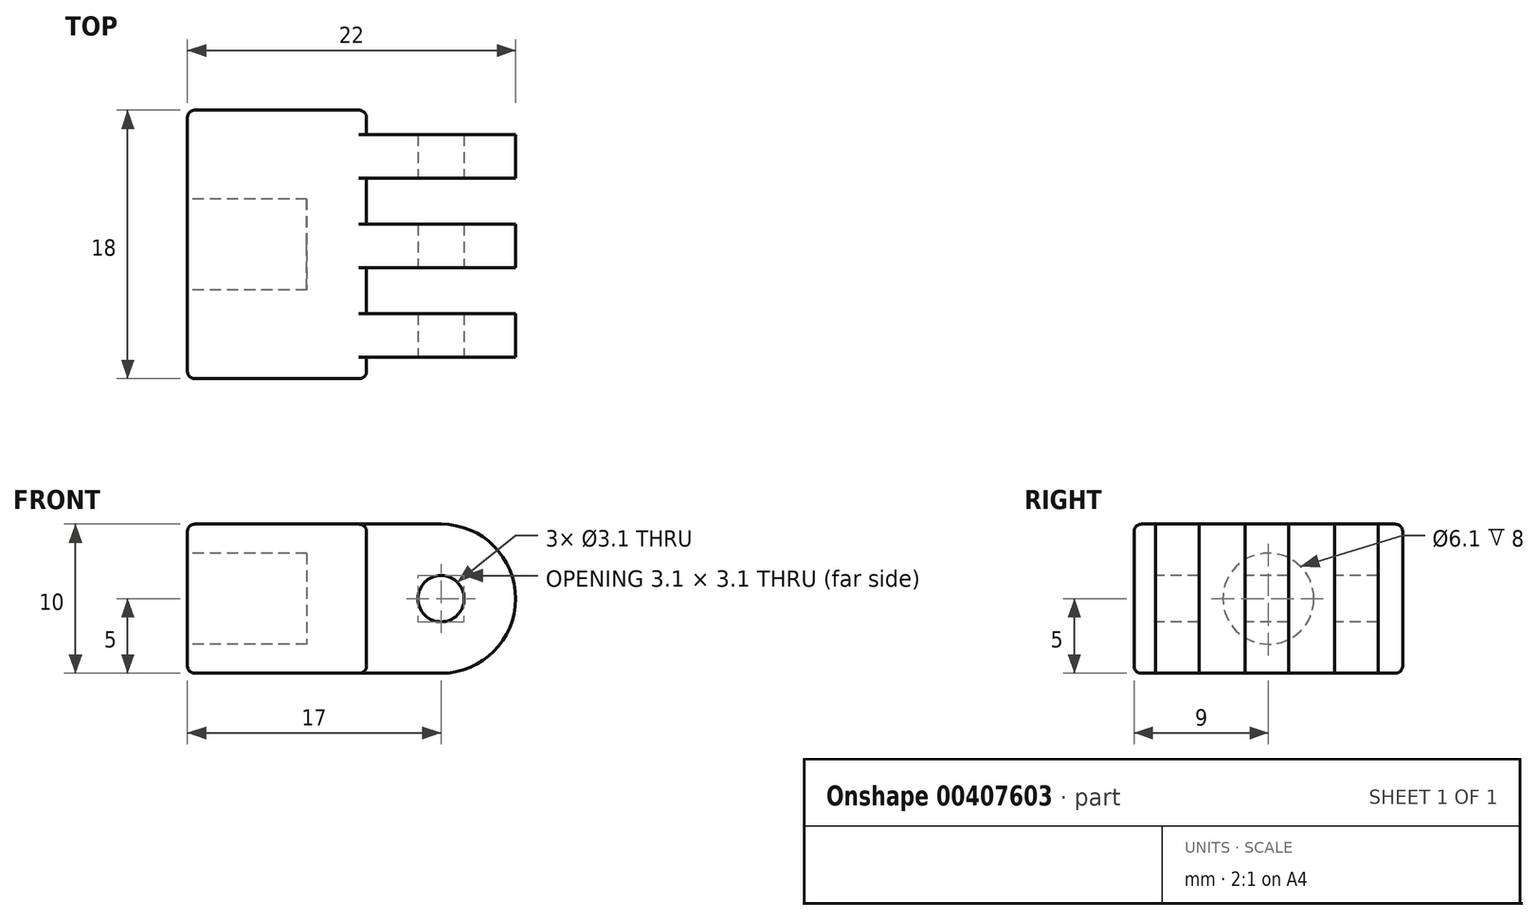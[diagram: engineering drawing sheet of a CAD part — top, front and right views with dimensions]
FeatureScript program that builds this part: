
annotation { "Feature Type Name" : "Feature", "Feature Type Description" : "" }
export const myFeature = defineFeature(function(context is Context, id is Id, definition is map)
    precondition{}
    {
        {
            var Q0;
            Q0=qCreatedBy(makeId("Top.planeOp"),FACE);
            var sketch = newSketch(context, id + "F0", { "sketchPlane" : qUnion([Q0])});
            skLineSegment(sketch, "E0.bottom", {"start": v(-6, 9) * mm, "end": v(6, 9) * mm});
            skLineSegment(sketch, "E0.top", {"start": v(-6, -9) * mm, "end": v(6, -9) * mm});
            skLineSegment(sketch, "E0.left", {"start": v(-6, 9) * mm, "end": v(-6, -9) * mm});
            skLineSegment(sketch, "E0.right", {"start": v(6, 9) * mm, "end": v(6, -9) * mm});
            skPoint(sketch, "E0.middle", {"position": v(0, 0) * mm});
            skLineSegment(sketch, "E1", {"start": v(0, 0) * mm, "end": v(19.14, 0) * mm, "construction": true});
            skLineSegment(sketch, "E2", {"start": v(6, 1.35) * mm, "end": v(16, 1.35) * mm});
            skLineSegment(sketch, "E3", {"start": v(16, 1.35) * mm, "end": v(16, -1.55) * mm});
            skLineSegment(sketch, "E4", {"start": v(16, -1.55) * mm, "end": v(6, -1.55) * mm});
            skLineSegment(sketch, "E5", {"start": v(6, 4.45) * mm, "end": v(16, 4.45) * mm});
            skLineSegment(sketch, "E6", {"start": v(16, 4.45) * mm, "end": v(16, 7.35) * mm});
            skLineSegment(sketch, "E7", {"start": v(16, 7.35) * mm, "end": v(6, 7.35) * mm});
            skLineSegment(sketch, "E8", {"start": v(6, -4.65) * mm, "end": v(16, -4.65) * mm});
            skLineSegment(sketch, "E9", {"start": v(16, -4.65) * mm, "end": v(16, -7.55) * mm});
            skLineSegment(sketch, "E10", {"start": v(16, -7.55) * mm, "end": v(6, -7.55) * mm});
            skSolve(sketch);
        }
        {
            var Q0;
            {var subQ1=sQuery(id+"F0.wireOp",EDGE,"E0.bottom");Q0=makeQuery(id+"F0.imprint","IMPRINT",FACE,{"disambiguationData":[TD([[makeQuery(id+"F0.imprint","IMPRINT",EDGE,{"derivedFrom":subQ1}),-1.0]])]});}
            var Q1;
            {var subQ0=sQuery(id+"F0.wireOp",EDGE,"E5");Q1=makeQuery(id+"F0.imprint","IMPRINT",FACE,{"disambiguationData":[TD([[makeQuery(id+"F0.imprint","IMPRINT",EDGE,{"derivedFrom":subQ0}),1.0]])]});}
            var Q2;
            {var subQ0=sQuery(id+"F0.wireOp",EDGE,"E2");Q2=makeQuery(id+"F0.imprint","IMPRINT",FACE,{"disambiguationData":[TD([[makeQuery(id+"F0.imprint","IMPRINT",EDGE,{"derivedFrom":subQ0}),-1.0]])]});}
            var Q3;
            {var subQ0=sQuery(id+"F0.wireOp",EDGE,"E8");Q3=makeQuery(id+"F0.imprint","IMPRINT",FACE,{"disambiguationData":[TD([[makeQuery(id+"F0.imprint","IMPRINT",EDGE,{"derivedFrom":subQ0}),-1.0]])]});}
            extrude(context, id + "F1", {"entities" : qUnion([Q0, Q1, Q2, Q3]), "depth" : 10 * mm});
        }
        {
            var Q0;
            Q0=makeQuery(id+"F1.opExtrude","SWEPT_FACE",FACE,{"disambiguationData":[OSD([sQuery(id+"F0.wireOp",EDGE,"E0.left")])]});
            var sketch = newSketch(context, id + "F2", { "sketchPlane" : qUnion([Q0])});
            skLineSegment(sketch, "E11", {"start": v(0, 0) * mm, "end": v(0, 10) * mm, "construction": true});
            skLineSegment(sketch, "E12", {"start": v(9, 5) * mm, "end": v(-9, 5) * mm, "construction": true});
            skCircle(sketch, "E13", {"center": v(0, 5) * mm, "radius": 3.05 * mm});
            skSolve(sketch);
        }
        {
            var Q0;
            Q0=makeQuery(id+"F2.imprint","IMPRINT",FACE,{"disambiguationData":[TD([[makeQuery(id+"F2.imprint","IMPRINT",EDGE,{"derivedFrom":sQuery(id+"F2.wireOp",EDGE,"E13")}),1.0]])]});
            extrude(context, id + "F3", {"entities" : qUnion([Q0]), "operationType" : NewBodyOperationType.REMOVE, "oppositeDirection" : true, "depth" : 8 * mm});
        }
        {
            var Q0;
            Q0=makeQuery(id+"F1.opExtrude","SWEPT_FACE",FACE,{"disambiguationData":[OSD([sQuery(id+"F0.wireOp",EDGE,"E10")])]});
            var sketch = newSketch(context, id + "F4", { "sketchPlane" : qUnion([Q0])});
            skLineSegment(sketch, "E14", {"start": v(11, 0) * mm, "end": v(11, 10) * mm, "construction": true});
            skLineSegment(sketch, "E15", {"start": v(16, 5) * mm, "end": v(6, 5) * mm, "construction": true});
            skCircle(sketch, "E16", {"center": v(11, 5) * mm, "radius": 1.55 * mm});
            skSolve(sketch);
        }
        {
            var Q0;
            Q0=makeQuery(id+"F4.imprint","IMPRINT",FACE,{"disambiguationData":[TD([[makeQuery(id+"F4.imprint","IMPRINT",EDGE,{"derivedFrom":sQuery(id+"F4.wireOp",EDGE,"E16")}),1.0]])]});
            extrude(context, id + "F5", {"entities" : qUnion([Q0]), "operationType" : NewBodyOperationType.REMOVE, "oppositeDirection" : true, "depth" : 25 * mm});
        }
        {
            var Q0;
            Q0=makeQuery(id+"F1.opExtrude","CAP_EDGE",EDGE,{"disambiguationData":[OSD([sQuery(id+"F0.wireOp",EDGE,"E0.left")])],"isStart":false});
            var Q1;
            Q1=makeQuery(id+"F1.opExtrude","CAP_EDGE",EDGE,{"disambiguationData":[OSD([sQuery(id+"F0.wireOp",EDGE,"E0.top")])],"isStart":false});
            var Q2;
            Q2=makeQuery(id+"F1.opExtrude","CAP_EDGE",EDGE,{"disambiguationData":[OSD([sQuery(id+"F0.wireOp",EDGE,"E0.bottom")])],"isStart":false});
            var Q3;
            Q3=makeQuery(id+"F1.opExtrude","SWEPT_EDGE",EDGE,{"disambiguationData":[OSD([sQuery(id+"F0.wireOp",EDGE,"E0.top"),sQuery(id+"F0.wireOp",EDGE,"E0.left")])]});
            var Q4;
            Q4=makeQuery(id+"F1.opExtrude","CAP_EDGE",EDGE,{"disambiguationData":[OSD([sQuery(id+"F0.wireOp",EDGE,"E0.left")])],"isStart":true});
            var Q5;
            Q5=makeQuery(id+"F1.opExtrude","SWEPT_EDGE",EDGE,{"disambiguationData":[OSD([sQuery(id+"F0.wireOp",EDGE,"E0.bottom"),sQuery(id+"F0.wireOp",EDGE,"E0.left")])]});
            var Q6;
            Q6=makeQuery(id+"F1.opExtrude","CAP_EDGE",EDGE,{"disambiguationData":[OSD([sQuery(id+"F0.wireOp",EDGE,"E0.bottom")])],"isStart":true});
            var Q7;
            Q7=makeQuery(id+"F1.opExtrude","CAP_EDGE",EDGE,{"disambiguationData":[OSD([sQuery(id+"F0.wireOp",EDGE,"E0.top")])],"isStart":true});
            var Q8;
            Q8=makeQuery(id+"F1.opExtrude","SWEPT_EDGE",EDGE,{"disambiguationData":[OSD([sQuery(id+"F0.wireOp",EDGE,"E0.top"),sQuery(id+"F0.wireOp",EDGE,"E0.right")])]});
            var Q9;
            {var subQ0=sQuery(id+"F0.wireOp",EDGE,"E0.right");Q9=makeQuery(id+"F1.opExtrude","CAP_EDGE",EDGE,{"disambiguationData":[OSD([subQ0]),TDD([makeQuery(id+"F0.imprint","IMPRINT",EDGE,{"disambiguationData":[TD([[makeQuery(id+"F0.imprint","INTERSECT",VERTEX,{"derivedFrom":[sQuery(id+"F0.wireOp",EDGE,"E0.top"),subQ0]}),1.0]])],"derivedFrom":subQ0})])],"isStart":true});}
            var Q10;
            {var subQ0=sQuery(id+"F0.wireOp",EDGE,"E0.right");Q10=makeQuery(id+"F1.opExtrude","CAP_EDGE",EDGE,{"disambiguationData":[OSD([subQ0]),TDD([makeQuery(id+"F0.imprint","IMPRINT",EDGE,{"disambiguationData":[TD([[makeQuery(id+"F0.imprint","INTERSECT",VERTEX,{"derivedFrom":[subQ0,sQuery(id+"F0.wireOp",EDGE,"E4")]}),-1.0]])],"derivedFrom":subQ0})])],"isStart":true});}
            var Q11;
            {var subQ0=sQuery(id+"F0.wireOp",EDGE,"E0.right");Q11=makeQuery(id+"F1.opExtrude","CAP_EDGE",EDGE,{"disambiguationData":[OSD([subQ0]),TDD([makeQuery(id+"F0.imprint","IMPRINT",EDGE,{"disambiguationData":[TD([[makeQuery(id+"F0.imprint","INTERSECT",VERTEX,{"derivedFrom":[subQ0,sQuery(id+"F0.wireOp",EDGE,"E2")]}),1.0]])],"derivedFrom":subQ0})])],"isStart":true});}
            var Q12;
            {var subQ0=sQuery(id+"F0.wireOp",EDGE,"E0.right");Q12=makeQuery(id+"F1.opExtrude","CAP_EDGE",EDGE,{"disambiguationData":[OSD([subQ0]),TDD([makeQuery(id+"F0.imprint","IMPRINT",EDGE,{"disambiguationData":[TD([[makeQuery(id+"F0.imprint","INTERSECT",VERTEX,{"derivedFrom":[sQuery(id+"F0.wireOp",EDGE,"E0.bottom"),subQ0]}),-1.0]])],"derivedFrom":subQ0})])],"isStart":true});}
            var Q13;
            Q13=makeQuery(id+"F1.opExtrude","SWEPT_EDGE",EDGE,{"disambiguationData":[OSD([sQuery(id+"F0.wireOp",EDGE,"E0.bottom"),sQuery(id+"F0.wireOp",EDGE,"E0.right")])]});
            var Q14;
            {var subQ0=sQuery(id+"F0.wireOp",EDGE,"E0.right");Q14=makeQuery(id+"F1.opExtrude","CAP_EDGE",EDGE,{"disambiguationData":[OSD([subQ0]),TDD([makeQuery(id+"F0.imprint","IMPRINT",EDGE,{"disambiguationData":[TD([[makeQuery(id+"F0.imprint","INTERSECT",VERTEX,{"derivedFrom":[sQuery(id+"F0.wireOp",EDGE,"E0.bottom"),subQ0]}),-1.0]])],"derivedFrom":subQ0})])],"isStart":false});}
            var Q15;
            {var subQ0=sQuery(id+"F0.wireOp",EDGE,"E0.right");Q15=makeQuery(id+"F1.opExtrude","CAP_EDGE",EDGE,{"disambiguationData":[OSD([subQ0]),TDD([makeQuery(id+"F0.imprint","IMPRINT",EDGE,{"disambiguationData":[TD([[makeQuery(id+"F0.imprint","INTERSECT",VERTEX,{"derivedFrom":[subQ0,sQuery(id+"F0.wireOp",EDGE,"E2")]}),1.0]])],"derivedFrom":subQ0})])],"isStart":false});}
            var Q16;
            {var subQ0=sQuery(id+"F0.wireOp",EDGE,"E0.right");Q16=makeQuery(id+"F1.opExtrude","CAP_EDGE",EDGE,{"disambiguationData":[OSD([subQ0]),TDD([makeQuery(id+"F0.imprint","IMPRINT",EDGE,{"disambiguationData":[TD([[makeQuery(id+"F0.imprint","INTERSECT",VERTEX,{"derivedFrom":[subQ0,sQuery(id+"F0.wireOp",EDGE,"E4")]}),-1.0]])],"derivedFrom":subQ0})])],"isStart":false});}
            var Q17;
            {var subQ0=sQuery(id+"F0.wireOp",EDGE,"E0.right");Q17=makeQuery(id+"F1.opExtrude","CAP_EDGE",EDGE,{"disambiguationData":[OSD([subQ0]),TDD([makeQuery(id+"F0.imprint","IMPRINT",EDGE,{"disambiguationData":[TD([[makeQuery(id+"F0.imprint","INTERSECT",VERTEX,{"derivedFrom":[sQuery(id+"F0.wireOp",EDGE,"E0.top"),subQ0]}),1.0]])],"derivedFrom":subQ0})])],"isStart":false});}
            fillet(context, id + "F6", {"entities" : qUnion([Q0, Q1, Q2, Q3, Q4, Q5, Q6, Q7, Q8, Q9, Q10, Q11, Q12, Q13, Q14, Q15, Q16, Q17]), "radius" : 0.5 * mm, "tangentPropagation" : true, "allowEdgeOverflow" : false});
        }
        {
            var Q0;
            Q0=makeQuery(id+"F1.opExtrude","CAP_EDGE",EDGE,{"disambiguationData":[OSD([sQuery(id+"F0.wireOp",EDGE,"E6")])],"isStart":true});
            var Q1;
            Q1=makeQuery(id+"F1.opExtrude","CAP_EDGE",EDGE,{"disambiguationData":[OSD([sQuery(id+"F0.wireOp",EDGE,"E6")])],"isStart":false});
            var Q2;
            Q2=makeQuery(id+"F1.opExtrude","CAP_EDGE",EDGE,{"disambiguationData":[OSD([sQuery(id+"F0.wireOp",EDGE,"E3")])],"isStart":false});
            var Q3;
            Q3=makeQuery(id+"F1.opExtrude","CAP_EDGE",EDGE,{"disambiguationData":[OSD([sQuery(id+"F0.wireOp",EDGE,"E3")])],"isStart":true});
            var Q4;
            Q4=makeQuery(id+"F1.opExtrude","CAP_EDGE",EDGE,{"disambiguationData":[OSD([sQuery(id+"F0.wireOp",EDGE,"E9")])],"isStart":true});
            var Q5;
            Q5=makeQuery(id+"F1.opExtrude","CAP_EDGE",EDGE,{"disambiguationData":[OSD([sQuery(id+"F0.wireOp",EDGE,"E9")])],"isStart":false});
            fillet(context, id + "F7", {"entities" : qUnion([Q0, Q1, Q2, Q3, Q4, Q5]), "radius" : 5 * mm, "tangentPropagation" : true, "allowEdgeOverflow" : false});
        }
    });
